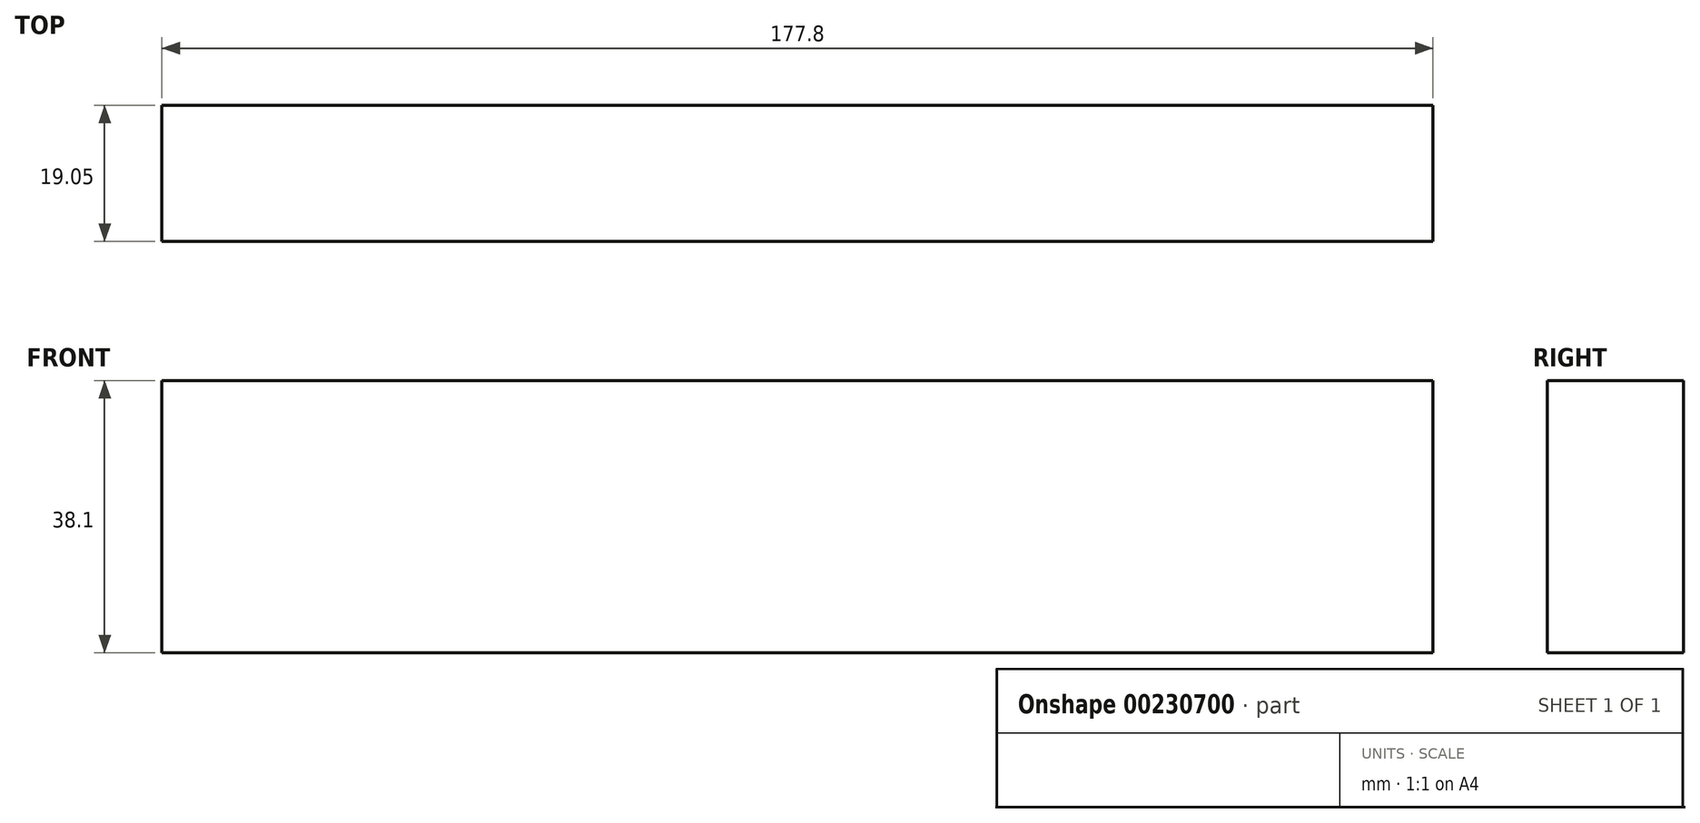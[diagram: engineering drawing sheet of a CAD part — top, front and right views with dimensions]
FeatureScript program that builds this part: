
annotation { "Feature Type Name" : "Feature", "Feature Type Description" : "" }
export const myFeature = defineFeature(function(context is Context, id is Id, definition is map)
    precondition{}
    {
        {
            var Q0;
            Q0=qCreatedBy(makeId("Right.planeOp"),FACE);
            var sketch = newSketch(context, id + "F0", { "sketchPlane" : qUnion([Q0])});
            skLineSegment(sketch, "E0.bottom", {"start": v(-11.67, 12.22) * mm, "end": v(7.38, 12.22) * mm});
            skLineSegment(sketch, "E0.top", {"start": v(-11.67, -25.88) * mm, "end": v(7.38, -25.88) * mm});
            skLineSegment(sketch, "E0.left", {"start": v(-11.67, 12.22) * mm, "end": v(-11.67, -25.88) * mm});
            skLineSegment(sketch, "E0.right", {"start": v(7.38, 12.22) * mm, "end": v(7.38, -25.88) * mm});
            skSolve(sketch);
        }
        {
            var Q0;
            Q0=makeQuery(id+"F0.imprint","IMPRINT",FACE,{"disambiguationData":[TD([[makeQuery(id+"F0.imprint","IMPRINT",EDGE,{"derivedFrom":sQuery(id+"F0.wireOp",EDGE,"E0.bottom")}),-1.0]])]});
            extrude(context, id + "F1", {"entities" : qUnion([Q0]), "depth" : 177.8 * mm});
        }
    });
